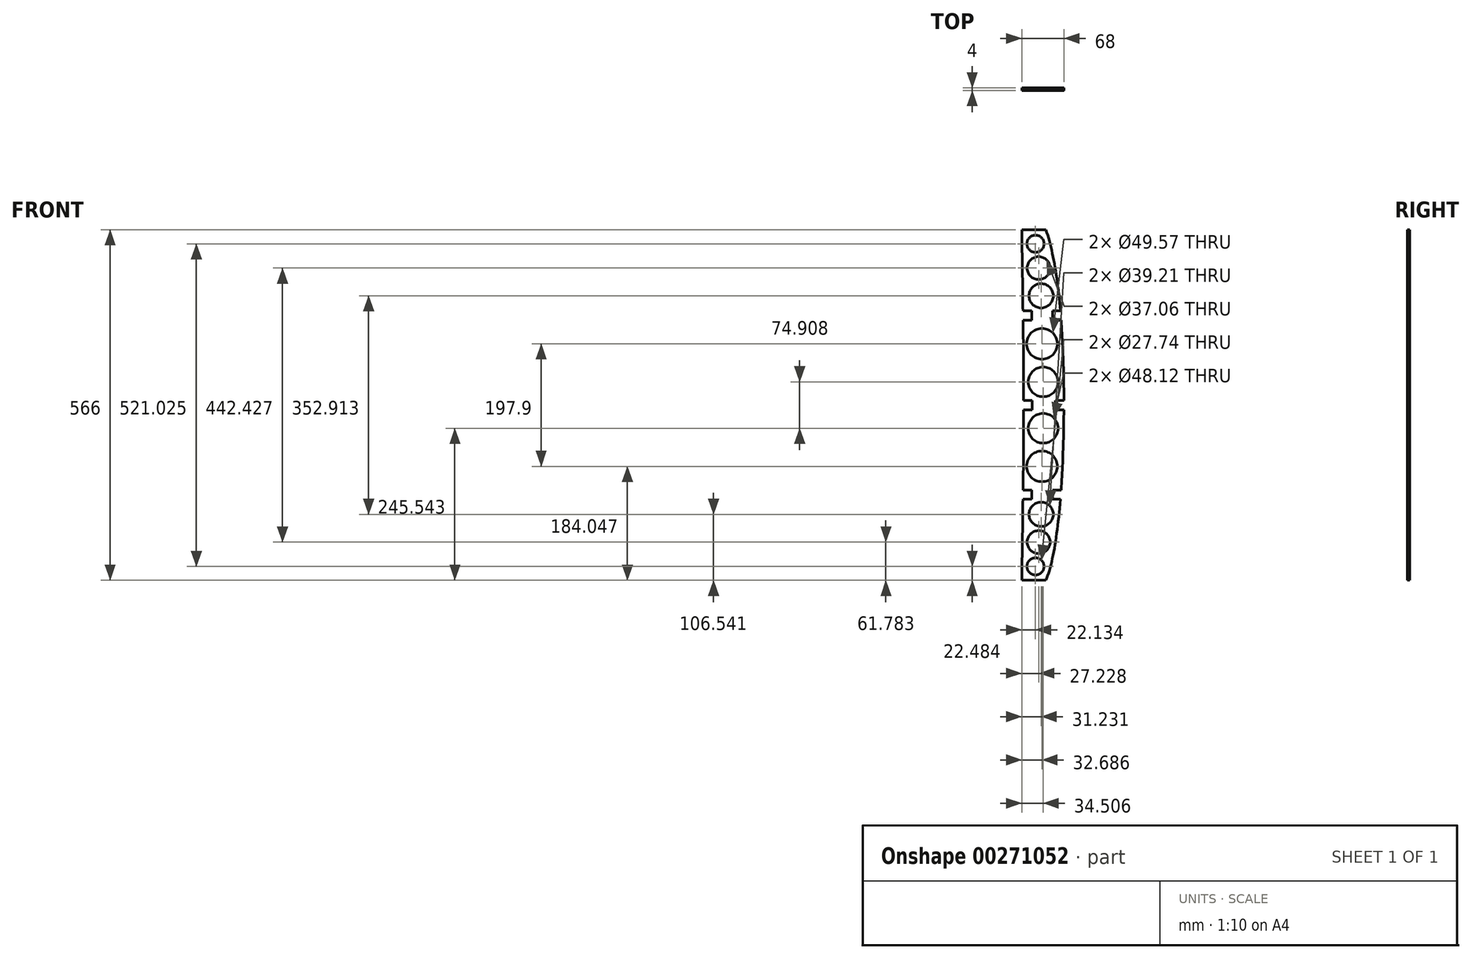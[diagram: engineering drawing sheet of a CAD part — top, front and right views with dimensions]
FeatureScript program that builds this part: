
annotation { "Feature Type Name" : "Feature", "Feature Type Description" : "" }
export const myFeature = defineFeature(function(context is Context, id is Id, definition is map)
    precondition{}
    {
        {
            var Q0;
            Q0=qCreatedBy(makeId("Front.planeOp"),FACE);
            var sketch = newSketch(context, id + "F0", { "sketchPlane" : qUnion([Q0])});
            skLineSegment(sketch, "E0", {"start": v(218.6, 129.32) * mm, "end": v(247.6, 129.32) * mm});
            skLineSegment(sketch, "E1", {"start": v(218.6, -436.68) * mm, "end": v(247.6, -436.68) * mm});
            skLineSegment(sketch, "E2", {"start": v(276.6, -153.68) * mm, "end": v(140.24, -153.68) * mm});
            skLineSegment(sketch, "E3", {"start": v(208.6, -436.68) * mm, "end": v(218.6, -436.68) * mm});
            skLineSegment(sketch, "E4", {"start": v(218.6, 129.32) * mm, "end": v(208.6, 129.32) * mm});
            skLineSegment(sketch, "E5", {"start": v(283.1, -9.18) * mm, "end": v(130.07, -9.18) * mm});
            skLineSegment(sketch, "E6", {"start": v(208.6, -436.68) * mm, "end": v(208.6, 129.32) * mm});
            skLineSegment(sketch, "E7", {"start": v(208.6, -153.68) * mm, "end": v(211.6, -153.68) * mm});
            skFitSpline(sketch, "E8", {"points": [v(247.6, 129.32) * mm, v(276.6, -153.68) * mm, v(247.6, -436.68) * mm], "startDerivative": vector(127.74, -362.42) * mm, "endDerivative": vector(-123.5, -294.55) * mm});
            skFitSpline(sketch, "E9", {"points": [v(208.6, 129.32) * mm, v(211.6, -153.68) * mm, v(208.6, -436.68) * mm], "startDerivative": vector(9, -566) * mm, "endDerivative": vector(-9, -566) * mm});
            skLineSegment(sketch, "E10", {"start": v(262.6, -153.68) * mm, "end": v(262.6, -146.18) * mm});
            skLineSegment(sketch, "E11", {"start": v(262.6, -146.18) * mm, "end": v(276.6, -146.18) * mm});
            skLineSegment(sketch, "E12", {"start": v(225.6, -146.18) * mm, "end": v(225.6, -153.68) * mm});
            skLineSegment(sketch, "E13", {"start": v(225.6, -146.18) * mm, "end": v(211.6, -146.18) * mm});
            skLineSegment(sketch, "E14.MirrorCS", {"start": v(262.6, -161.18) * mm, "end": v(276.6, -161.18) * mm});
            skLineSegment(sketch, "E15.MirrorCS", {"start": v(262.6, -153.68) * mm, "end": v(262.6, -161.18) * mm});
            skLineSegment(sketch, "E16.MirrorCS", {"start": v(225.6, -161.18) * mm, "end": v(225.6, -153.68) * mm});
            skLineSegment(sketch, "E17.MirrorCS", {"start": v(225.6, -161.18) * mm, "end": v(211.6, -161.18) * mm});
            skLineSegment(sketch, "E18", {"start": v(258.2, -9.18) * mm, "end": v(258.2, -1.68) * mm});
            skLineSegment(sketch, "E19", {"start": v(258.2, -1.68) * mm, "end": v(271.02, -1.68) * mm});
            skLineSegment(sketch, "E20", {"start": v(258.2, -9.18) * mm, "end": v(258.2, -16.68) * mm});
            skLineSegment(sketch, "E21", {"start": v(258.2, -16.68) * mm, "end": v(272.2, -16.68) * mm});
            skLineSegment(sketch, "E22", {"start": v(224.71, -16.68) * mm, "end": v(224.71, -1.68) * mm});
            skLineSegment(sketch, "E23", {"start": v(224.71, -16.68) * mm, "end": v(210.71, -16.68) * mm});
            skLineSegment(sketch, "E24", {"start": v(224.71, -1.68) * mm, "end": v(210.53, -1.68) * mm});
            skCircle(sketch, "E25", {"center": v(243.1, -116.23) * mm, "radius": 24.06 * mm});
            skCircle(sketch, "E26", {"center": v(241.29, -54.73) * mm, "radius": 24.79 * mm});
            skCircle(sketch, "E27", {"center": v(239.83, 22.77) * mm, "radius": 19.6 * mm});
            skCircle(sketch, "E28", {"center": v(235.83, 67.53) * mm, "radius": 18.53 * mm});
            skCircle(sketch, "E29", {"center": v(230.73, 106.83) * mm, "radius": 13.87 * mm});
            skCircle(sketch, "E30.MirrorC", {"center": v(243.1, -191.14) * mm, "radius": 24.06 * mm});
            skCircle(sketch, "E31.MirrorC", {"center": v(241.29, -252.63) * mm, "radius": 24.79 * mm});
            skCircle(sketch, "E32.MirrorC", {"center": v(239.83, -330.14) * mm, "radius": 19.6 * mm});
            skCircle(sketch, "E33.MirrorC", {"center": v(235.83, -374.9) * mm, "radius": 18.53 * mm});
            skCircle(sketch, "E34.MirrorC", {"center": v(230.73, -414.2) * mm, "radius": 13.87 * mm});
            skLineSegment(sketch, "E35.MirrorCS", {"start": v(258.2, -305.68) * mm, "end": v(271.02, -305.68) * mm});
            skLineSegment(sketch, "E36.MirrorCS", {"start": v(258.2, -298.18) * mm, "end": v(258.2, -290.68) * mm});
            skLineSegment(sketch, "E37.MirrorCS", {"start": v(224.71, -290.68) * mm, "end": v(210.71, -290.68) * mm});
            skLineSegment(sketch, "E38.MirrorCS", {"start": v(258.2, -290.68) * mm, "end": v(272.2, -290.68) * mm});
            skLineSegment(sketch, "E39.MirrorCS", {"start": v(224.71, -305.68) * mm, "end": v(210.53, -305.68) * mm});
            skLineSegment(sketch, "E40.MirrorCS", {"start": v(224.71, -290.68) * mm, "end": v(224.71, -305.68) * mm});
            skLineSegment(sketch, "E41.MirrorCS", {"start": v(258.2, -298.18) * mm, "end": v(258.2, -305.68) * mm});
            skSolve(sketch);
        }
        {
            var Q0;
            {var subQ5=sQuery(id+"F0.wireOp",EDGE,"E0");Q0=makeQuery(id+"F0.imprint","IMPRINT",FACE,{"disambiguationData":[TD([[makeQuery(id+"F0.imprint","IMPRINT",EDGE,{"derivedFrom":subQ5}),-1.0]])]});}
            var Q1;
            {var subQ3=sQuery(id+"F0.wireOp",EDGE,"E10");Q1=makeQuery(id+"F0.imprint","IMPRINT",FACE,{"disambiguationData":[TD([[makeQuery(id+"F0.imprint","IMPRINT",EDGE,{"derivedFrom":subQ3}),1.0]])]});}
            var Q2;
            {var subQ5=sQuery(id+"F0.wireOp",EDGE,"E1");Q2=makeQuery(id+"F0.imprint","IMPRINT",FACE,{"disambiguationData":[TD([[makeQuery(id+"F0.imprint","IMPRINT",EDGE,{"derivedFrom":subQ5}),1.0]])]});}
            extrude(context, id + "F1", {"entities" : qUnion([Q0, Q1, Q2]), "depth" : 4 * mm});
        }
    });
